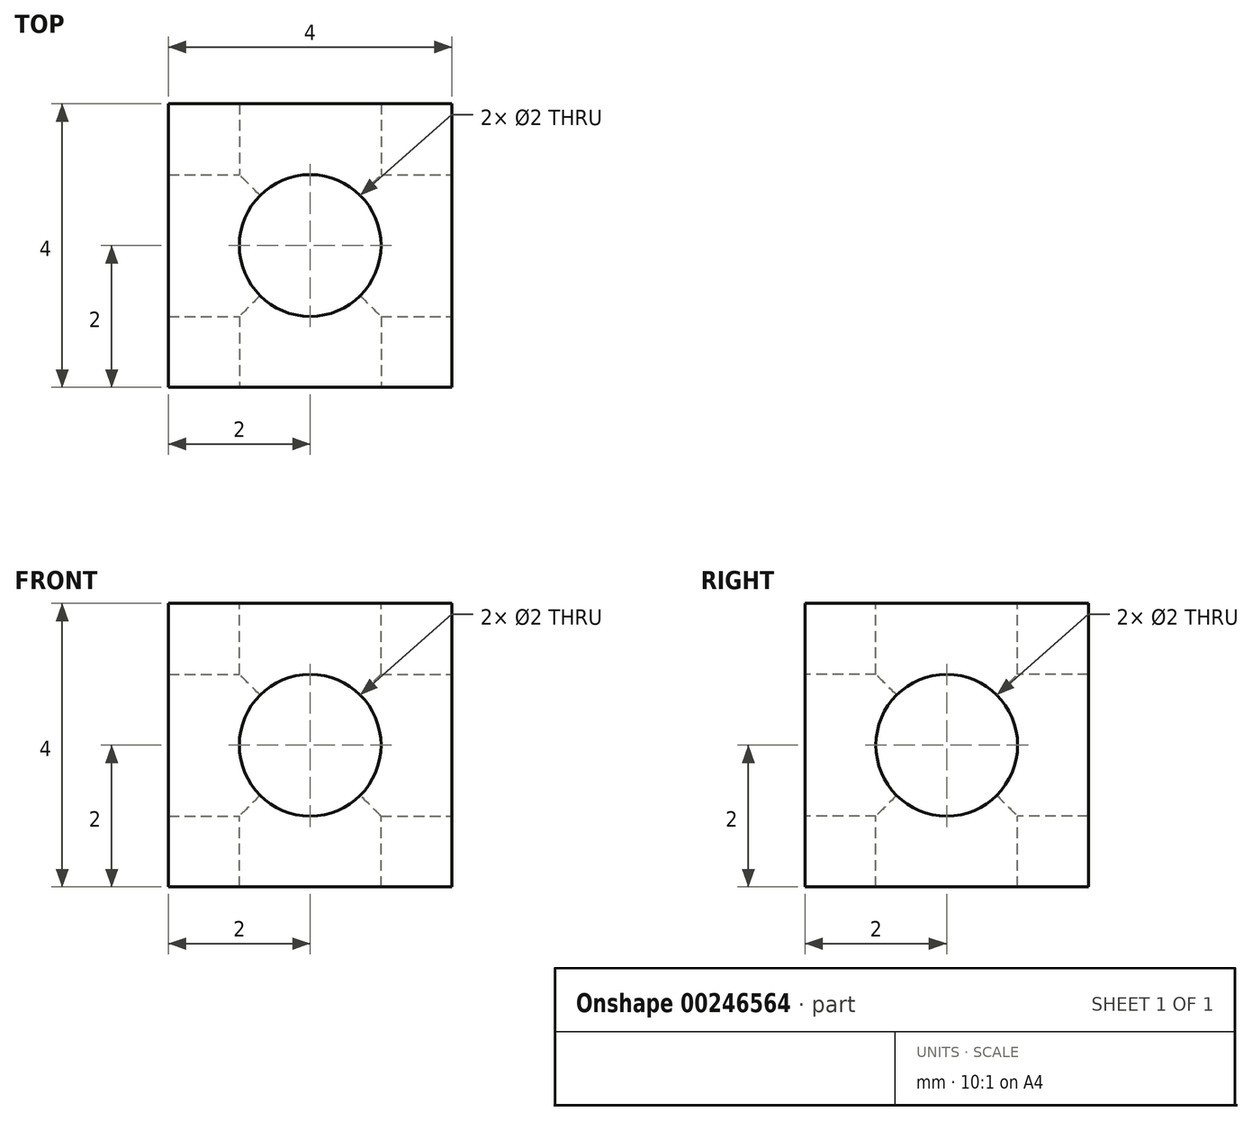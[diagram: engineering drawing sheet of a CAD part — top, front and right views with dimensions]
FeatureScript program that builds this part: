
annotation { "Feature Type Name" : "Feature", "Feature Type Description" : "" }
export const myFeature = defineFeature(function(context is Context, id is Id, definition is map)
    precondition{}
    {
        {
            var Q0;
            Q0=qCreatedBy(makeId("Top.planeOp"),FACE);
            var sketch = newSketch(context, id + "F0", { "sketchPlane" : qUnion([Q0])});
            skLineSegment(sketch, "E0.bottom", {"start": v(0, 0) * mm, "end": v(4, 0) * mm});
            skLineSegment(sketch, "E0.top", {"start": v(0, 4) * mm, "end": v(4, 4) * mm});
            skLineSegment(sketch, "E0.left", {"start": v(0, 0) * mm, "end": v(0, 4) * mm});
            skLineSegment(sketch, "E0.right", {"start": v(4, 0) * mm, "end": v(4, 4) * mm});
            skSolve(sketch);
        }
        {
            var Q0;
            Q0 = qSketchRegion(id + "F0", true);
            extrude(context, id + "F1", {"entities" : qUnion([Q0]), "depth" : 4 * mm});
        }
        {
            var Q0;
            Q0=makeQuery(id+"F1.opExtrude","CAP_FACE",FACE,{"disambiguationData":[OSD([sQuery(id+"F0.wireOp",EDGE,"E0.bottom"),sQuery(id+"F0.wireOp",EDGE,"E0.top"),sQuery(id+"F0.wireOp",EDGE,"E0.left"),sQuery(id+"F0.wireOp",EDGE,"E0.right")])],"isStart":false});
            var sketch = newSketch(context, id + "F2", { "sketchPlane" : qUnion([Q0])});
            skCircle(sketch, "E1", {"center": v(2, 2) * mm, "radius": 1 * mm});
            skSolve(sketch);
        }
        {
            var Q0;
            Q0=makeQuery(id+"F1.opExtrude","SWEPT_FACE",FACE,{"disambiguationData":[OSD([sQuery(id+"F0.wireOp",EDGE,"E0.right")])]});
            var sketch = newSketch(context, id + "F3", { "sketchPlane" : qUnion([Q0])});
            skSolve(sketch);
        }
        {
            var Q0;
            Q0=makeQuery(id+"F2.imprint","IMPRINT",FACE,{"disambiguationData":[TD([[makeQuery(id+"F2.imprint","IMPRINT",EDGE,{"derivedFrom":sQuery(id+"F2.wireOp",EDGE,"E1")}),1.0]])]});
            extrude(context, id + "F4", {"entities" : qUnion([Q0]), "operationType" : NewBodyOperationType.REMOVE, "oppositeDirection" : true, "depth" : 25 * mm});
        }
        {
            var Q0;
            Q0=makeQuery(id+"F1.opExtrude","SWEPT_FACE",FACE,{"disambiguationData":[OSD([sQuery(id+"F0.wireOp",EDGE,"E0.bottom")])]});
            var sketch = newSketch(context, id + "F5", { "sketchPlane" : qUnion([Q0])});
            skCircle(sketch, "E2", {"center": v(2, 2) * mm, "radius": 1 * mm});
            skSolve(sketch);
        }
        {
            var Q0;
            Q0=makeQuery(id+"F5.imprint","IMPRINT",FACE,{"disambiguationData":[TD([[makeQuery(id+"F5.imprint","IMPRINT",EDGE,{"derivedFrom":sQuery(id+"F5.wireOp",EDGE,"E2")}),1.0]])]});
            extrude(context, id + "F6", {"entities" : qUnion([Q0]), "operationType" : NewBodyOperationType.REMOVE, "oppositeDirection" : true, "depth" : 25 * mm});
        }
        {
            var Q0;
            {var subQ0=sQuery(id+"F0.wireOp",EDGE,"E0.right");Q0=makeQuery(id+"F3.imprint","IMPRINT",FACE,{"disambiguationData":[TD([[makeQuery(id+"F3.imprint","IMPRINT",EDGE,{"derivedFrom":makeQuery(id+"F1.opExtrude","CAP_EDGE",EDGE,{"disambiguationData":[OSD([subQ0])],"isStart":true})}),1.0]])]});}
            var sketch = newSketch(context, id + "F7", { "sketchPlane" : qUnion([Q0])});
            skPoint(sketch, "E3.0", {"position": v(4, 4) * mm});
            skPoint(sketch, "E3.1", {"position": v(4, 0) * mm});
            skPoint(sketch, "E3.2", {"position": v(0, 4) * mm});
            skCircle(sketch, "E4", {"center": v(2, 2) * mm, "radius": 1 * mm});
            skSolve(sketch);
        }
        {
            var Q0;
            Q0 = qSketchRegion(id + "F7", true);
            extrude(context, id + "F8", {"entities" : qUnion([Q0]), "operationType" : NewBodyOperationType.REMOVE, "oppositeDirection" : true, "depth" : 25 * mm});
        }
    });
